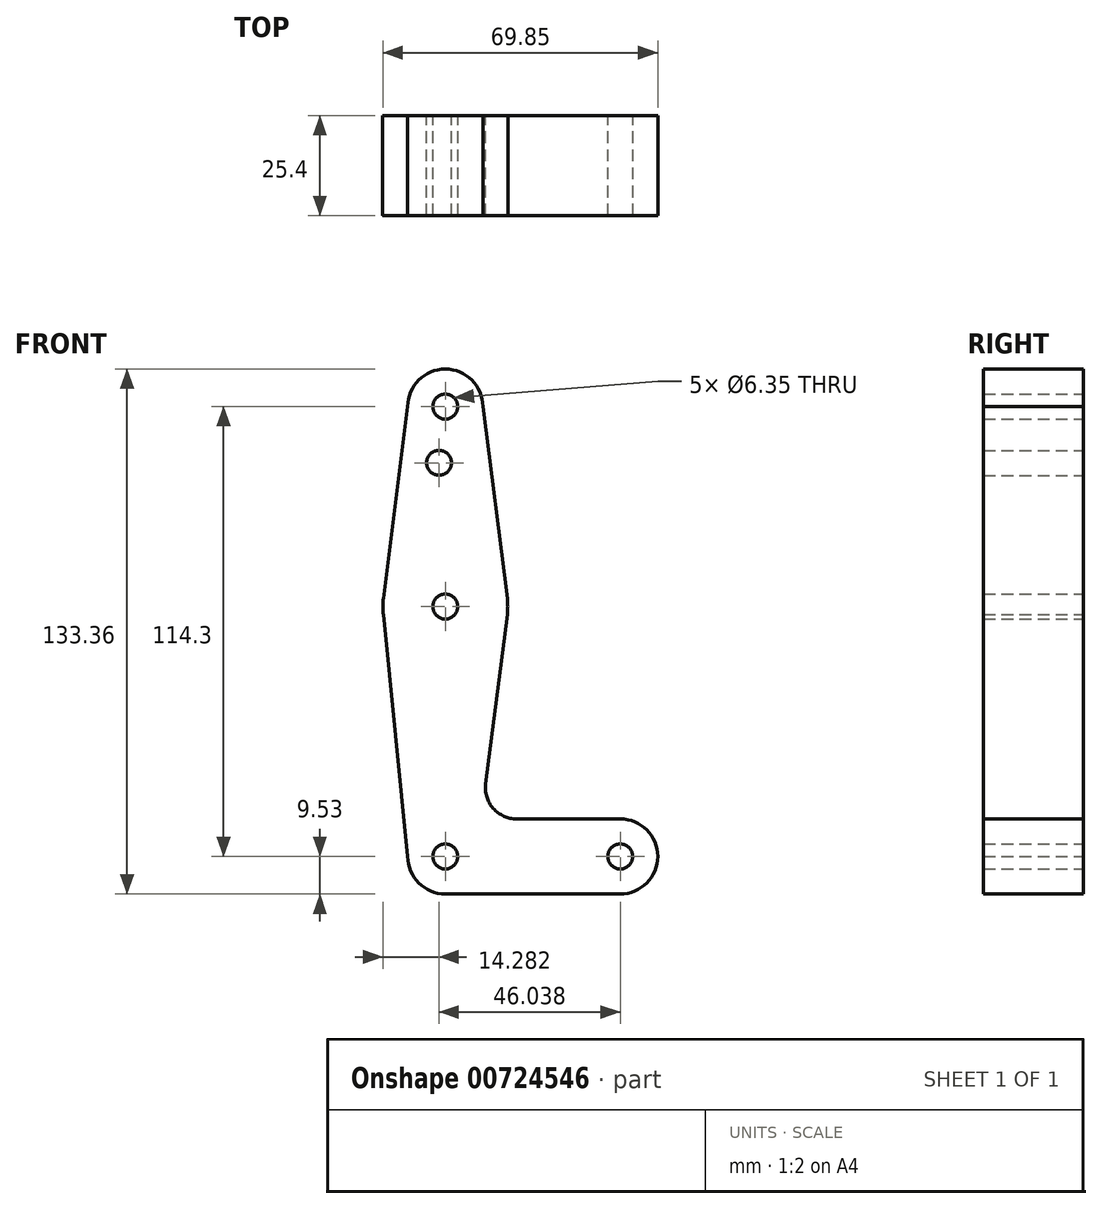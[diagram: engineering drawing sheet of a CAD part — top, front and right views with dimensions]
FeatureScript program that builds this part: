
annotation { "Feature Type Name" : "Feature", "Feature Type Description" : "" }
export const myFeature = defineFeature(function(context is Context, id is Id, definition is map)
    precondition{}
    {
        {
            var Q0;
            Q0=qCreatedBy(makeId("Front.planeOp"),FACE);
            var sketch = newSketch(context, id + "F0", { "sketchPlane" : qUnion([Q0])});
            skLineSegment(sketch, "E0", {"start": v(0, 0) * mm, "end": v(0, 114.3) * mm, "construction": true});
            skLineSegment(sketch, "E1", {"start": v(0, 0) * mm, "end": v(44.45, 0) * mm, "construction": true});
            skCircle(sketch, "E2", {"center": v(0, 114.3) * mm, "radius": 9.53 * mm});
            skCircle(sketch, "E3", {"center": v(0, 63.5) * mm, "radius": 15.88 * mm});
            skCircle(sketch, "E4", {"center": v(0, 0) * mm, "radius": 9.53 * mm});
            skCircle(sketch, "E5", {"center": v(44.45, 0) * mm, "radius": 9.53 * mm});
            skLineSegment(sketch, "E6", {"start": v(18.15, 9.52) * mm, "end": v(44.45, 9.52) * mm});
            skLineSegment(sketch, "E7", {"start": v(-9.53, 114.3) * mm, "end": v(-15.75, 65.5) * mm});
            skLineSegment(sketch, "E8", {"start": v(9.53, 114.3) * mm, "end": v(16, 63.5) * mm});
            skLineSegment(sketch, "E9", {"start": v(-9.53, 0) * mm, "end": v(-15.75, 61.5) * mm});
            skLineSegment(sketch, "E10", {"start": v(15.75, 61.5) * mm, "end": v(10.26, 18.48) * mm});
            skLineSegment(sketch, "E11", {"start": v(0, -9.53) * mm, "end": v(44.45, -9.52) * mm});
            skCircle(sketch, "E12", {"center": v(0, 63.5) * mm, "radius": 3.18 * mm});
            skCircle(sketch, "E13", {"center": v(0, 114.3) * mm, "radius": 3.18 * mm});
            skCircle(sketch, "E14", {"center": v(0, 0) * mm, "radius": 3.18 * mm});
            skCircle(sketch, "E15", {"center": v(44.45, 0) * mm, "radius": 3.18 * mm});
            skCircle(sketch, "E16", {"center": v(-1.59, 100.03) * mm, "radius": 3.18 * mm});
            skArc(sketch, "E17.filletArc", {"start": v(10.26, 18.48) * mm, "mid": v(12.18, 12.22) * mm, "end": v(18.15, 9.53) * mm});
            skSolve(sketch);
        }
        {
            var Q0;
            Q0 = qSketchRegion(id + "F0", true);
            extrude(context, id + "F1", {"entities" : qUnion([Q0]), "depth" : 25.4 * mm, "offsetDistance" : 25.4 * mm});
        }
    });
